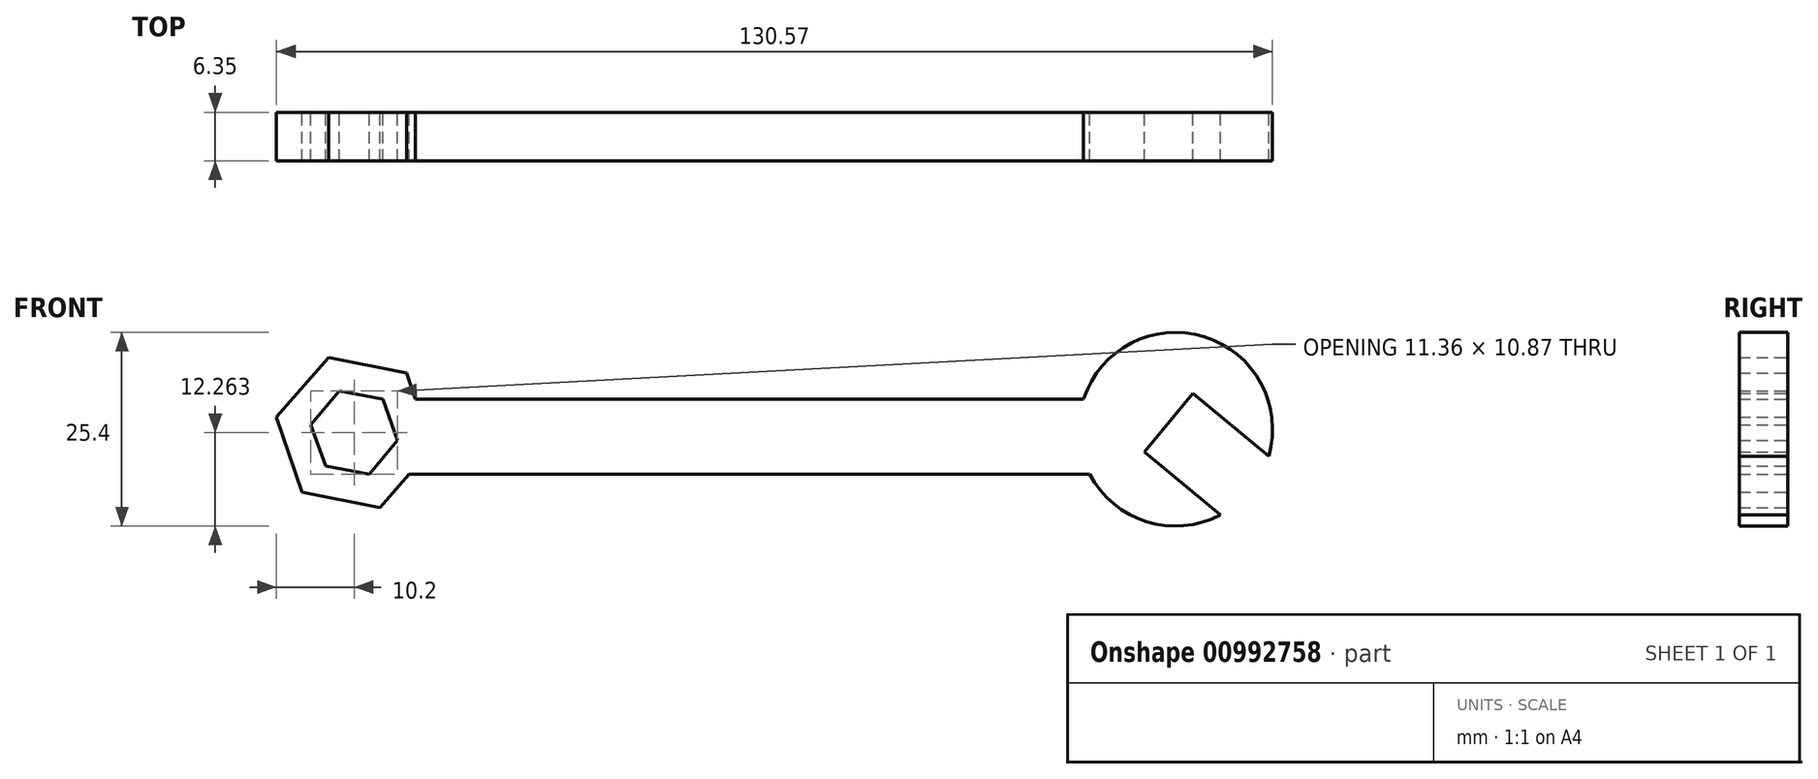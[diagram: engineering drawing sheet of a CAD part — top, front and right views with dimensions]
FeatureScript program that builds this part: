
annotation { "Feature Type Name" : "Feature", "Feature Type Description" : "" }
export const myFeature = defineFeature(function(context is Context, id is Id, definition is map)
    precondition{}
    {
        {
            var Q0;
            Q0=qCreatedBy(makeId("Front.planeOp"),FACE);
            var sketch = newSketch(context, id + "F0", { "sketchPlane" : qUnion([Q0])});
            skCircle(sketch, "E0", {"center": v(80.93, 47.04) * mm, "radius": 12.7 * mm});
            skCircle(sketch, "E1.cCircle", {"center": v(-26.74, 46.6) * mm, "radius": 5 * mm, "construction": true});
            skLineSegment(sketch, "E1.0", {"start": v(-32.42, 47.63) * mm, "end": v(-28.7, 52.04) * mm});
            skLineSegment(sketch, "E1.1", {"start": v(-28.7, 52.04) * mm, "end": v(-23.01, 51.01) * mm});
            skLineSegment(sketch, "E1.2", {"start": v(-23.01, 51.01) * mm, "end": v(-21.06, 45.58) * mm});
            skLineSegment(sketch, "E1.3", {"start": v(-21.06, 45.58) * mm, "end": v(-24.79, 41.17) * mm});
            skLineSegment(sketch, "E1.4", {"start": v(-24.79, 41.17) * mm, "end": v(-30.47, 42.2) * mm});
            skLineSegment(sketch, "E1.5", {"start": v(-30.47, 42.2) * mm, "end": v(-32.42, 47.63) * mm});
            skPoint(sketch, "E1.0.midPoint", {"position": v(-30.56, 49.83) * mm});
            skLineSegment(sketch, "E2.bottom", {"start": v(-24.79, 41.17) * mm, "end": v(76.81, 41.17) * mm});
            skLineSegment(sketch, "E2.top", {"start": v(-24.79, 51.01) * mm, "end": v(76.81, 51.01) * mm});
            skLineSegment(sketch, "E2.left", {"start": v(-24.79, 41.17) * mm, "end": v(-24.79, 51.01) * mm});
            skLineSegment(sketch, "E2.right", {"start": v(76.81, 41.17) * mm, "end": v(76.81, 51.01) * mm});
            skLineSegment(sketch, "E3", {"start": v(93.13, 43.51) * mm, "end": v(83.2, 51.76) * mm});
            skLineSegment(sketch, "E4", {"start": v(83.2, 51.76) * mm, "end": v(76.81, 44.06) * mm});
            skPoint(sketch, "E4.endSnap0", {"position": v(76.81, 46.1) * mm});
            skLineSegment(sketch, "E5", {"start": v(76.81, 44.06) * mm, "end": v(86.8, 35.77) * mm});
            skCircle(sketch, "E6.cCircle", {"center": v(-26.74, 46.6) * mm, "radius": 9 * mm, "construction": true});
            skLineSegment(sketch, "E6.0", {"start": v(-36.94, 48.62) * mm, "end": v(-30.1, 56.44) * mm});
            skLineSegment(sketch, "E6.1", {"start": v(-30.1, 56.44) * mm, "end": v(-19.9, 54.43) * mm});
            skLineSegment(sketch, "E6.2", {"start": v(-19.9, 54.43) * mm, "end": v(-16.54, 44.6) * mm});
            skLineSegment(sketch, "E6.3", {"start": v(-16.54, 44.6) * mm, "end": v(-23.39, 36.77) * mm});
            skLineSegment(sketch, "E6.4", {"start": v(-23.39, 36.77) * mm, "end": v(-33.58, 38.78) * mm});
            skLineSegment(sketch, "E6.5", {"start": v(-33.58, 38.78) * mm, "end": v(-36.94, 48.62) * mm});
            skPoint(sketch, "E6.0.midPoint", {"position": v(-33.52, 52.53) * mm});
            skSolve(sketch);
        }
        {
            var Q0;
            {var subQ5=sQuery(id+"F0.wireOp",EDGE,"E0");var subQ7=sQuery(id+"F0.wireOp",EDGE,"E2.bottom");var subQ8=makeQuery(id+"F0.imprint","INTERSECT",VERTEX,{"derivedFrom":[subQ5,subQ7]});Q0=makeQuery(id+"F0.imprint","IMPRINT",FACE,{"disambiguationData":[TD([[makeQuery(id+"F0.imprint","IMPRINT",EDGE,{"disambiguationData":[TD([[subQ8,1.0]])],"derivedFrom":subQ5}),-1.0]])]});}
            var Q1;
            {var subQ1=sQuery(id+"F0.wireOp",EDGE,"E2.bottom");var subQ6=sQuery(id+"F0.wireOp",EDGE,"E0");var subQ8=makeQuery(id+"F0.imprint","INTERSECT",VERTEX,{"derivedFrom":[subQ6,subQ1]});Q1=makeQuery(id+"F0.imprint","IMPRINT",FACE,{"disambiguationData":[TD([[makeQuery(id+"F0.imprint","IMPRINT",EDGE,{"disambiguationData":[TD([[subQ8,1.0]])],"derivedFrom":subQ6}),1.0]])]});}
            var Q2;
            {var subQ0=sQuery(id+"F0.wireOp",EDGE,"E3");Q2=makeQuery(id+"F0.imprint","IMPRINT",FACE,{"disambiguationData":[TD([[makeQuery(id+"F0.imprint","IMPRINT",EDGE,{"derivedFrom":subQ0}),-1.0]])]});}
            var Q3;
            {var subQ0=sQuery(id+"F0.wireOp",EDGE,"E5");Q3=makeQuery(id+"F0.imprint","IMPRINT",FACE,{"disambiguationData":[TD([[makeQuery(id+"F0.imprint","IMPRINT",EDGE,{"derivedFrom":subQ0}),-1.0]])]});}
            var Q4;
            {var subQ1=sQuery(id+"F0.wireOp",EDGE,"E1.2");Q4=makeQuery(id+"F0.imprint","IMPRINT",FACE,{"disambiguationData":[TD([[makeQuery(id+"F0.imprint","IMPRINT",EDGE,{"derivedFrom":subQ1}),1.0]])]});}
            var Q5;
            Q5=makeQuery(id+"F0.imprint","IMPRINT",FACE,{"disambiguationData":[TD([[makeQuery(id+"F0.imprint","IMPRINT",EDGE,{"derivedFrom":sQuery(id+"F0.wireOp",EDGE,"E1.0")}),1.0]])]});
            extrude(context, id + "F1", {"entities" : qUnion([Q0, Q1, Q2, Q3, Q4, Q5]), "depth" : 6.35 * mm, "offsetDistance" : 25.4 * mm});
        }
    });
